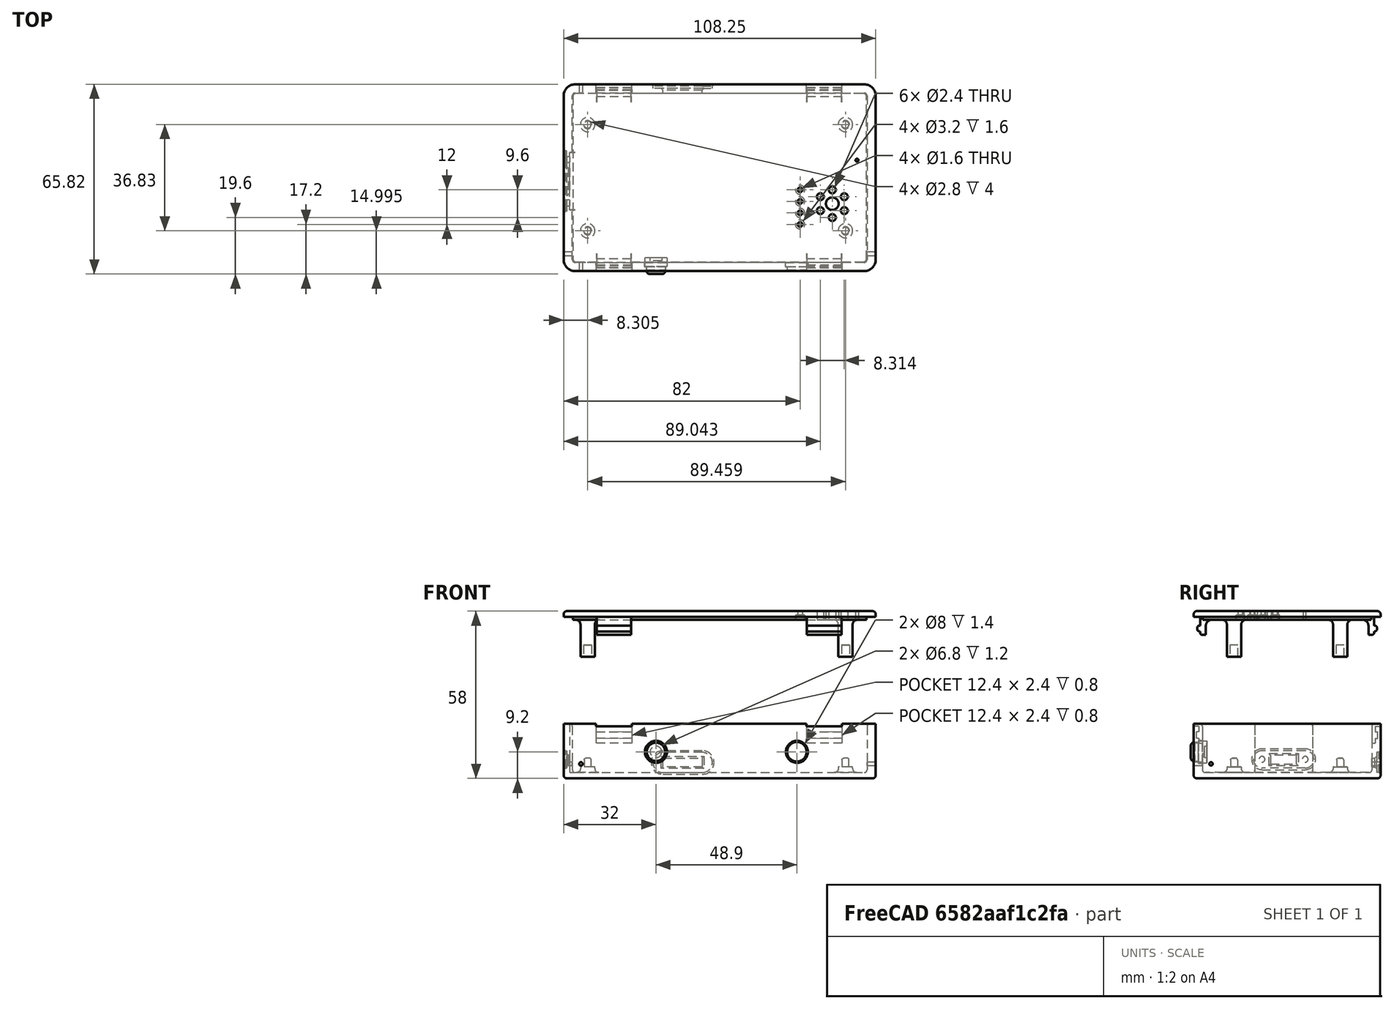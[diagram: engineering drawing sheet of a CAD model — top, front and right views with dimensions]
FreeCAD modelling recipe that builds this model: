
FCSTD DOCUMENT  (FreeCAD 0.17R13541 (Git))
Label: Variometer-Case
License: All rights reserved
LicenseURL: http://en.wikipedia.org/wiki/All_rights_reserved
objects: Sketcher::SketchObject×29, PartDesign::Pocket×17, PartDesign::Fillet×17, PartDesign::Plane×12, PartDesign::Pad×11, PartDesign::Body×4, Mesh::Feature×4, PartDesign::ShapeBinder×3, PartDesign::Chamfer×3
note: 124 computed .brp shape members not serialized (recipe doc carries the construction recipe); baked Part::Feature solids carry a one-line shape summary decoded from their .brp

FEATURE [Sketcher::SketchObject] Sketch  label="MasterSketch"
  MapMode = 5
  Support = -> [XY_Plane]
  sketch-geometry (27):
    g0: LineSegment StartX=0 StartY=58.42 StartZ=0 EndX=101.85 EndY=58.42 EndZ=0
    g1: LineSegment StartX=101.85 StartY=58.42 StartZ=0 EndX=101.85 EndY=0 EndZ=0
    g2: LineSegment StartX=101.85 StartY=0 StartZ=0 EndX=0 EndY=0 EndZ=0
    g3: LineSegment StartX=0 StartY=0 StartZ=0 EndX=0 EndY=58.42 EndZ=0
    g4: Circle CenterX=5.105 CenterY=10.795 CenterZ=0 NormalX=0 NormalY=0 NormalZ=1 AngleXU=0 Radius=2.5
    g5: Circle CenterX=5.105 CenterY=47.625 CenterZ=0 NormalX=0 NormalY=0 NormalZ=1 AngleXU=0 Radius=2.5
    g6: Circle CenterX=94.564 CenterY=10.795 CenterZ=0 NormalX=0 NormalY=0 NormalZ=1 AngleXU=0 Radius=2.5
    g7: Circle CenterX=94.564 CenterY=47.625 CenterZ=0 NormalX=0 NormalY=0 NormalZ=1 AngleXU=0 Radius=2.5
    g8: LineSegment StartX=28.3 StartY=53.4492 StartZ=0 EndX=28.3 EndY=63.3867 EndZ=0
    g9: LineSegment StartX=11.3 StartY=63.3867 StartZ=0 EndX=11.3 EndY=53.4492 EndZ=0
    g10: Circle CenterX=90 CenterY=20.2 CenterZ=0 NormalX=0 NormalY=0 NormalZ=1 AngleXU=0 Radius=7
    g11: Circle CenterX=78.8 CenterY=25 CenterZ=0 NormalX=0 NormalY=0 NormalZ=1 AngleXU=0 Radius=1
    g12: Circle CenterX=78.8 CenterY=21 CenterZ=0 NormalX=0 NormalY=0 NormalZ=1 AngleXU=0 Radius=1
    g13: Circle CenterX=78.8 CenterY=17 CenterZ=0 NormalX=0 NormalY=0 NormalZ=1 AngleXU=0 Radius=1
    g14: Circle CenterX=78.8 CenterY=13 CenterZ=0 NormalX=0 NormalY=0 NormalZ=1 AngleXU=0 Radius=1
    g15: Circle CenterX=98.56 CenterY=35.28 CenterZ=0 NormalX=0 NormalY=0 NormalZ=1 AngleXU=0 Radius=1
    g16: LineSegment StartX=46.46 StartY=63.8315 StartZ=0 EndX=46.46 EndY=53.6528 EndZ=0
    g17: LineSegment StartX=31.26 StartY=53.6528 StartZ=0 EndX=31.26 EndY=63.3799 EndZ=0
    g18: LineSegment StartX=164.118 StartY=59.2092 StartZ=0 EndX=164.118 EndY=40.2092 EndZ=0
    g19: LineSegment StartX=176.88 StartY=59.5541 StartZ=0 EndX=176.88 EndY=42.5541 EndZ=0
    g20: LineSegment StartX=-10.0374 StartY=20.5 StartZ=0 EndX=4.83678 EndY=20.5 EndZ=0
    g21: LineSegment StartX=-10.1738 StartY=28 StartZ=0 EndX=4.42739 EndY=28 EndZ=0
    g22: LineSegment StartX=-10.0374 StartY=35.5 StartZ=0 EndX=4.56386 EndY=35.5 EndZ=0
    g23: LineSegment StartX=28.8 StartY=5.89163 StartZ=0 EndX=28.8 EndY=-5.34826 EndZ=0
    g24: LineSegment StartX=77.7 StartY=5.89163 StartZ=0 EndX=77.7 EndY=-5.48472 EndZ=0
    g25: LineSegment StartX=8 StartY=6.13746 StartZ=0 EndX=8 EndY=-25.1864 EndZ=0
    g26: LineSegment StartX=81 StartY=5.59162 StartZ=0 EndX=81 EndY=-24.8827 EndZ=0
  constraints (67):
    c: Coincident(g0,g1)
    c: Coincident(g1,g2)
    c: Coincident(g2,g3)
    c: Coincident(g3,g0)
    c: Horizontal(g0)
    c: Horizontal(g2)
    c: Vertical(g1)
    c: Vertical(g3)
    c: DistanceX(g0,g0) = 101.85  'PCB_Width'
    c: DistanceY(g1,g1) = 58.42  'PCB_Height'
    c: Coincident(g2,g-1)
    c: DistanceX(g-1,g4) = 5.105
    c: Vertical(g4,g5)
    c: DistanceY(g-1,g4) = 10.795
    c: DistanceY(g-1,g5) = 47.625
    c: DistanceX(g-1,g6) = 94.564
    c: Vertical(g6,g7)
    c: Horizontal(g4,g6)
    c: Horizontal(g5,g7)
    c: Radius(g5) = 2.5  'PCBSupporterRadius'
    c: Equal(g5,g4)
    c: Equal(g5,g6)
    c: Equal(g5,g7)
    c: Vertical(g8)
    c: Vertical(g9)
    c: DistanceX(g-1,g10) = 90
    c: DistanceY(g-1,g10) = 20.2
    c: Radius(g10) = 7
    c: Vertical(g14,g13)
    c: Vertical(g13,g12)
    c: Vertical(g12,g11)
    c: DistanceX(g-1,g14) = 78.8
    c: Radius(g14) = 1
    c: Equal(g14,g13)
    c: Equal(g14,g12)
    c: Equal(g14,g11)
    c: DistanceY(g1,g14) = 13
    c: DistanceY(g1,g13) = 17
    c: DistanceY(g1,g12) = 21
    c: DistanceY(g1,g11) = 25
    c: DistanceX(g-1,g15) = 98.56
    c: DistanceY(g1,g15) = 35.28
    c: Vertical(g16)
    c: Vertical(g17)
    c: DistanceX(g-1,g17) = 31.26  'BT_X1'
    c: Radius(g15) = 1
    c: Vertical(g18)
    c: Vertical(g19)
    c: DistanceY(g18,g18) = 19  'totalHeight'
    c: DistanceY(g19,g19) = 17  'innerDepth'
    c: Horizontal(g20)
    c: Horizontal(g21)
    c: Horizontal(g22)
    c: DistanceY(g-1,g20) = 20.5  'ledGreeHeight'
    c: DistanceY(g-1,g21) = 28  'USBPos'
    c: DistanceY(g-1,g22) = 35.5  'RedLEDPos'
    c: Vertical(g23)
    c: Vertical(g24)
    c: DistanceX(g-1,g23) = 28.8
    c: DistanceX(g-1,g24) = 77.7
    c: DistanceX(g0,g16) = 46.46  'BT_X2'
    c: DistanceX(g0,g9) = 11.3  'IMU_X1'
    c: DistanceX(g0,g8) = 28.3  'IMU_X2'
    c: Vertical(g25)
    c: Vertical(g26)
    c: DistanceX(g-1,g25) = 8  'Locker_X1'
    c: DistanceX(g-1,g26) = 81  'Locker_X2'
FEATURE [PartDesign::Body] Body  label="MasterBlock"
  Group = -> [Sketch]
  Origin = -> Origin
FEATURE [PartDesign::ShapeBinder] ShapeBinder  label="BodyShapeBinder"
  Support = -> [Sketch]
FEATURE [Sketcher::SketchObject] Sketch001  label="Outer"
  ExternalGeometry = -> [ShapeBinder]
  MapMode = 5
  Support = -> [XY_Plane001]
  sketch-geometry (4):
    g0: LineSegment StartX=-3.2 StartY=61.62 StartZ=0 EndX=105.05 EndY=61.62 EndZ=0
    g1: LineSegment StartX=105.05 StartY=61.62 StartZ=0 EndX=105.05 EndY=-3.2 EndZ=0
    g2: LineSegment StartX=105.05 StartY=-3.2 StartZ=0 EndX=-3.2 EndY=-3.2 EndZ=0
    g3: LineSegment StartX=-3.2 StartY=-3.2 StartZ=0 EndX=-3.2 EndY=61.62 EndZ=0
  constraints (12):
    c: Coincident(g0,g1)
    c: Coincident(g1,g2)
    c: Coincident(g2,g3)
    c: Coincident(g3,g0)
    c: Horizontal(g0)
    c: Horizontal(g2)
    c: Vertical(g1)
    c: Vertical(g3)
    c: DistanceY(g2,g-1) = 3.2
    c: DistanceX(g2,g-1) = 3.2
    c: DistanceX(g-3,g0) = 3.2
    c: DistanceY(g-3,g0) = 3.2
FEATURE [PartDesign::Pad] Pad  label="OuterBlock"
  Length = 19
  Length2 = 100
  Profile = -> Sketch001
  Type = 0
  expr: Length = 19
FEATURE [PartDesign::Plane] DatumPlane  label="UpperPlane"
  MapMode = 45
  Placement = pos=(50.925,29.21,19) rot=(0,0,1;1.5708rad)
  Support = -> [Pad]
FEATURE [Sketcher::SketchObject] Sketch002  label="Inner"
  ExternalGeometry = -> [Pad]
  MapMode = 5
  Placement = pos=(50.925,29.21,19) rot=(0,0,1;1.5708rad)
  Support = -> [DatumPlane]
  sketch-geometry (4):
    g0: LineSegment StartX=-29.41 StartY=51.125 StartZ=0 EndX=29.41 EndY=51.125 EndZ=0
    g1: LineSegment StartX=29.41 StartY=51.125 StartZ=0 EndX=29.41 EndY=-51.125 EndZ=0
    g2: LineSegment StartX=29.41 StartY=-51.125 StartZ=0 EndX=-29.41 EndY=-51.125 EndZ=0
    g3: LineSegment StartX=-29.41 StartY=-51.125 StartZ=0 EndX=-29.41 EndY=51.125 EndZ=0
  constraints (12):
    c: Coincident(g0,g1)
    c: Coincident(g1,g2)
    c: Coincident(g2,g3)
    c: Coincident(g3,g0)
    c: Horizontal(g0)
    c: Horizontal(g2)
    c: Vertical(g1)
    c: Vertical(g3)
    c: DistanceY(g0,g-3) = 3
    c: DistanceX(g-3,g0) = 3
    c: DistanceX(g1,g-4) = 3
    c: DistanceY(g-4,g1) = 3
FEATURE [PartDesign::Pocket] Pocket  label="InnerBlock"
  BaseFeature = -> Pad
  Length = 17
  Length2 = 100
  Profile = -> Sketch002
  Type = 0
FEATURE [PartDesign::Plane] DatumPlane001  label="InnerBottom"
  MapMode = 5
  Placement = pos=(0,0,2) rot=(0,0,1;0rad)
  Support = -> [Pocket]
FEATURE [Sketcher::SketchObject] Sketch003
  ExternalGeometry = -> [ShapeBinder]
  MapMode = 5
  Placement = pos=(0,0,2) rot=(0,0,1;0rad)
  Support = -> [DatumPlane001]
  sketch-geometry (4):
    g0: Circle CenterX=5.105 CenterY=47.625 CenterZ=0 NormalX=0 NormalY=0 NormalZ=1 AngleXU=0 Radius=2.5
    g1: Circle CenterX=94.564 CenterY=47.625 CenterZ=0 NormalX=0 NormalY=0 NormalZ=1 AngleXU=0 Radius=2.5
    g2: Circle CenterX=94.564 CenterY=10.795 CenterZ=0 NormalX=0 NormalY=0 NormalZ=1 AngleXU=0 Radius=2.5
    g3: Circle CenterX=5.105 CenterY=10.795 CenterZ=0 NormalX=0 NormalY=0 NormalZ=1 AngleXU=0 Radius=2.5
  constraints (8):
    c: Coincident(g0,g-5)
    c: Coincident(g1,g-4)
    c: Coincident(g2,g-3)
    c: Coincident(g3,g-6)
    c: Equal(g3,g0)
    c: Equal(g0,g1)
    c: Equal(g1,g2)
    c: Radius(g3) = 2.5
FEATURE [PartDesign::Pad] Pad001  label="PCBSupporter"
  BaseFeature = -> Pocket
  Length = 2
  Length2 = 100
  Profile = -> Sketch003
  Type = 0
FEATURE [PartDesign::Plane] DatumPlane002  label="PCBPlane"
  MapMode = 5
  Placement = pos=(0,0,4) rot=(0,0,1;0rad)
  Support = -> [Pad001]
FEATURE [Sketcher::SketchObject] Sketch004
  ExternalGeometry = -> [Pad001]
  MapMode = 5
  Placement = pos=(0,0,4) rot=(0,0,1;0rad)
  Support = -> [DatumPlane002]
  sketch-geometry (4):
    g0: Circle CenterX=5.105 CenterY=47.625 CenterZ=0 NormalX=0 NormalY=0 NormalZ=1 AngleXU=0 Radius=1.2
    g1: Circle CenterX=94.564 CenterY=47.625 CenterZ=0 NormalX=0 NormalY=0 NormalZ=1 AngleXU=0 Radius=1.2
    g2: Circle CenterX=94.564 CenterY=10.795 CenterZ=0 NormalX=0 NormalY=0 NormalZ=1 AngleXU=0 Radius=1.2
    g3: Circle CenterX=5.105 CenterY=10.795 CenterZ=0 NormalX=0 NormalY=0 NormalZ=1 AngleXU=0 Radius=1.2
  constraints (8):
    c: Coincident(g0,g-6)
    c: Coincident(g1,g-3)
    c: Coincident(g3,g-5)
    c: Coincident(g-4,g2)
    c: Equal(g0,g3)
    c: Equal(g3,g2)
    c: Equal(g2,g1)
    c: Radius(g0) = 1.2
FEATURE [PartDesign::Pad] Pad002  label="PCBHole"
  BaseFeature = -> Pad001
  Length = 3
  Length2 = 100
  Profile = -> Sketch004
  Type = 0
FEATURE [PartDesign::Plane] DatumPlane003  label="LeftSideInnerPlane"
  MapMode = 5
  Placement = pos=(0,58.62,0) rot=(1,0,0;1.5708rad)
  Support = -> [Pad002]
FEATURE [PartDesign::Plane] DatumPlane004  label="RightSideInnerPlane"
  MapMode = 5
  Placement = pos=(0,-0.2,0) rot=(0,0.707107,0.707107;3.14159rad)
  Support = -> [Pad002]
FEATURE [PartDesign::Plane] DatumPlane005  label="LowerSideInnerPlane"
  MapMode = 5
  Placement = pos=(-0.2,0,0) rot=(0.57735,0.57735,0.57735;2.0944rad)
  Support = -> [Pad002]
FEATURE [Sketcher::SketchObject] Sketch005  label="LeftSideInnerHoles"
  ExternalGeometry = -> [ShapeBinder,Pad002]
  MapMode = 5
  Placement = pos=(0,58.62,0) rot=(1,0,0;1.5708rad)
  Support = -> [DatumPlane003]
  sketch-geometry (12):
    g0: LineSegment StartX=8 StartY=19 StartZ=0 EndX=20.4 EndY=19 EndZ=0
    g1: LineSegment StartX=20.4 StartY=19 StartZ=0 EndX=20.4 EndY=18 EndZ=0
    g2: LineSegment StartX=20.4 StartY=18 StartZ=0 EndX=8 EndY=18 EndZ=0
    g3: LineSegment StartX=8 StartY=18 StartZ=0 EndX=8 EndY=19 EndZ=0
    g4: LineSegment StartX=81 StartY=19 StartZ=0 EndX=93.4 EndY=19 EndZ=0
    g5: LineSegment StartX=93.4 StartY=19 StartZ=0 EndX=93.4 EndY=18 EndZ=0
    g6: LineSegment StartX=93.4 StartY=18 StartZ=0 EndX=81 EndY=18 EndZ=0
    g7: LineSegment StartX=81 StartY=18 StartZ=0 EndX=81 EndY=19 EndZ=0
    g8: LineSegment StartX=31.26 StartY=7 StartZ=0 EndX=44.86 EndY=7 EndZ=0
    g9: LineSegment StartX=44.86 StartY=7 StartZ=0 EndX=44.86 EndY=4 EndZ=0
    g10: LineSegment StartX=44.86 StartY=4 StartZ=0 EndX=31.26 EndY=4 EndZ=0
    g11: LineSegment StartX=31.26 StartY=4 StartZ=0 EndX=31.26 EndY=7 EndZ=0
  constraints (36):
    c: Coincident(g0,g1)
    c: Coincident(g1,g2)
    c: Coincident(g2,g3)
    c: Coincident(g3,g0)
    c: Horizontal(g0)
    c: Horizontal(g2)
    c: Vertical(g1)
    c: Vertical(g3)
    c: Coincident(g4,g5)
    c: Coincident(g5,g6)
    c: Coincident(g6,g7)
    c: Coincident(g7,g4)
    c: Horizontal(g4)
    c: Horizontal(g6)
    c: Vertical(g5)
    c: Vertical(g7)
    c: Coincident(g8,g9)
    c: Coincident(g9,g10)
    c: Coincident(g10,g11)
    c: Coincident(g11,g8)
    c: Horizontal(g8)
    c: Horizontal(g10)
    c: Vertical(g9)
    c: Vertical(g11)
    c: Vertical(g-5,g2)
    c: Vertical(g-7,g6)
    c: Equal(g0,g4)
    c: Equal(g1,g5)
    c: Tangent(g0,g-6) = 1.5708
    c: PointOnObject(g4,g-6)
    c: Distance(g1) = 1
    c: Distance(g0) = 12.4
    c: Vertical(g-3,g10)
    c: DistanceY(g9,g9) = 3
    c: DistanceY(g-4,g9) = 4
    c: DistanceX(g8,g8) = 13.6
FEATURE [PartDesign::Pocket] Pocket001  label="LeftSideThroughHole"
  BaseFeature = -> Pad002
  Length = 5
  Length2 = 100
  Profile = -> Sketch005
  Type = 1
FEATURE [Sketcher::SketchObject] Sketch006  label="RightSideInnerHoles"
  ExternalGeometry = -> [ShapeBinder,Pocket001]
  MapMode = 5
  Placement = pos=(0,-0.2,0) rot=(0,0.707107,0.707107;3.14159rad)
  Support = -> [DatumPlane004]
  sketch-geometry (10):
    g0: LineSegment StartX=-93.4 StartY=19 StartZ=0 EndX=-81 EndY=19 EndZ=0
    g1: LineSegment StartX=-81 StartY=19 StartZ=0 EndX=-81 EndY=18 EndZ=0
    g2: LineSegment StartX=-81 StartY=18 StartZ=0 EndX=-93.4 EndY=18 EndZ=0
    g3: LineSegment StartX=-93.4 StartY=18 StartZ=0 EndX=-93.4 EndY=19 EndZ=0
    g4: LineSegment StartX=-20.4 StartY=19 StartZ=0 EndX=-8 EndY=19 EndZ=0
    g5: LineSegment StartX=-8 StartY=19 StartZ=0 EndX=-8 EndY=18 EndZ=0
    g6: LineSegment StartX=-8 StartY=18 StartZ=0 EndX=-20.4 EndY=18 EndZ=0
    g7: LineSegment StartX=-20.4 StartY=18 StartZ=0 EndX=-20.4 EndY=19 EndZ=0
    g8: Circle CenterX=-77.7 CenterY=9.2 CenterZ=0 NormalX=0 NormalY=0 NormalZ=1 AngleXU=0 Radius=3.4
    g9: Circle CenterX=-28.8 CenterY=9.2 CenterZ=0 NormalX=0 NormalY=0 NormalZ=1 AngleXU=0 Radius=3.4
  constraints (30):
    c: Coincident(g0,g1)
    c: Coincident(g1,g2)
    c: Coincident(g2,g3)
    c: Coincident(g3,g0)
    c: Horizontal(g0)
    c: Horizontal(g2)
    c: Vertical(g1)
    c: Vertical(g3)
    c: Coincident(g4,g5)
    c: Coincident(g5,g6)
    c: Coincident(g6,g7)
    c: Coincident(g7,g4)
    c: Horizontal(g4)
    c: Horizontal(g6)
    c: Vertical(g5)
    c: Vertical(g7)
    c: PointOnObject(g0,g-7)
    c: PointOnObject(g4,g-7)
    c: Vertical(g-6,g1)
    c: Vertical(g-5,g5)
    c: Equal(g7,g3)
    c: DistanceY(g1,g1) = 1
    c: DistanceX(g0,g0) = 12.4
    c: Equal(g8,g9)
    c: Radius(g9) = 3.4
    c: Equal(g4,g0)
    c: Vertical(g-3,g8)
    c: Vertical(g-4,g9)
    c: Horizontal(g8,g9)
    c: DistanceY(g-4,g9) = 9.2
FEATURE [PartDesign::Pocket] Pocket002  label="RightSideThroughHole"
  BaseFeature = -> Pocket001
  Length = 5
  Length2 = 100
  Profile = -> Sketch006
  Type = 1
FEATURE [Sketcher::SketchObject] Sketch007  label="FrontSideInnderHoles"
  ExternalGeometry = -> [ShapeBinder]
  MapMode = 5
  Placement = pos=(-0.2,0,0) rot=(0.57735,0.57735,0.57735;2.0944rad)
  Support = -> [DatumPlane005]
  sketch-geometry (8):
    g0: Circle CenterX=20.5 CenterY=6.6 CenterZ=0 NormalX=0 NormalY=0 NormalZ=1 AngleXU=0 Radius=1
    g1: Circle CenterX=35.5 CenterY=6.6 CenterZ=0 NormalX=0 NormalY=0 NormalZ=1 AngleXU=0 Radius=1
    g2: LineSegment StartX=23.5 StartY=8 StartZ=0 EndX=32.5 EndY=8 EndZ=0
    g3: LineSegment StartX=32.5 StartY=8 StartZ=0 EndX=32.5 EndY=5 EndZ=0
    g4: LineSegment StartX=32.5 StartY=5 StartZ=0 EndX=23.5 EndY=5 EndZ=0
    g5: LineSegment StartX=23.5 StartY=5 StartZ=0 EndX=23.5 EndY=8 EndZ=0
    g6: LineSegment [constr] StartX=28 StartY=0 StartZ=0 EndX=28 EndY=13.3312 EndZ=0
    g7: LineSegment [constr] StartX=13.8871 StartY=5 StartZ=0 EndX=41.4899 EndY=5 EndZ=0
  constraints (22):
    c: Coincident(g2,g3)
    c: Coincident(g3,g4)
    c: Coincident(g4,g5)
    c: Coincident(g5,g2)
    c: Horizontal(g2)
    c: Horizontal(g4)
    c: Vertical(g3)
    c: Vertical(g5)
    c: Coincident(g6,g-3)
    c: Vertical(g6)
    c: Horizontal(g7)
    c: DistanceY(g-4,g7) = 5
    c: Symmetric(g2,g2,g6)
    c: DistanceX(g2,g2) = 9
    c: Vertical(g1,g-4)
    c: Vertical(g-5,g0)
    c: Horizontal(g0,g1)
    c: Equal(g0,g1)
    c: Radius(g0) = 1
    c: PointOnObject(g3,g7)
    c: DistanceY(g3,g3) = 3
    c: DistanceY(g4,g0) = 1.6
FEATURE [PartDesign::Pocket] Pocket003  label="FrontSideThroughHole"
  BaseFeature = -> Pocket002
  Length = 5
  Length2 = 100
  Profile = -> Sketch007
  Type = 1
FEATURE [PartDesign::Plane] DatumPlane006  label="RightSideOuterPlane"
  MapMode = 5
  Placement = pos=(0,61.62,0) rot=(0,0.707107,0.707107;3.14159rad)
  Support = -> [Pocket003]
FEATURE [PartDesign::Plane] DatumPlane007  label="LowerSideOuterPlane"
  MapMode = 5
  Placement = pos=(-3.2,0,0) rot=(0.57735,-0.57735,-0.57735;2.0944rad)
  Support = -> [Pocket003]
FEATURE [Sketcher::SketchObject] Sketch008  label="LockerHole"
  ExternalGeometry = -> [Pocket003]
  MapMode = 5
  Placement = pos=(50.925,29.21,19) rot=(0,0,1;1.5708rad)
  Support = -> [DatumPlane]
  sketch-geometry (16):
    g0: LineSegment StartX=-30.61 StartY=42.925 StartZ=0 EndX=-29.41 EndY=42.925 EndZ=0
    g1: LineSegment StartX=-29.41 StartY=42.925 StartZ=0 EndX=-29.41 EndY=30.525 EndZ=0
    g2: LineSegment StartX=-29.41 StartY=30.525 StartZ=0 EndX=-30.61 EndY=30.525 EndZ=0
    g3: LineSegment StartX=-30.61 StartY=30.525 StartZ=0 EndX=-30.61 EndY=42.925 EndZ=0
    g4: LineSegment StartX=29.41 StartY=42.925 StartZ=0 EndX=30.61 EndY=42.925 EndZ=0
    g5: LineSegment StartX=30.61 StartY=42.925 StartZ=0 EndX=30.61 EndY=30.525 EndZ=0
    g6: LineSegment StartX=30.61 StartY=30.525 StartZ=0 EndX=29.41 EndY=30.525 EndZ=0
    g7: LineSegment StartX=29.41 StartY=30.525 StartZ=0 EndX=29.41 EndY=42.925 EndZ=0
    g8: LineSegment StartX=29.41 StartY=-30.075 StartZ=0 EndX=30.61 EndY=-30.075 EndZ=0
    g9: LineSegment StartX=30.61 StartY=-30.075 StartZ=0 EndX=30.61 EndY=-42.475 EndZ=0
    g10: LineSegment StartX=30.61 StartY=-42.475 StartZ=0 EndX=29.41 EndY=-42.475 EndZ=0
    g11: LineSegment StartX=29.41 StartY=-42.475 StartZ=0 EndX=29.41 EndY=-30.075 EndZ=0
    g12: LineSegment StartX=-29.41 StartY=-30.075 StartZ=0 EndX=-30.61 EndY=-30.075 EndZ=0
    g13: LineSegment StartX=-30.61 StartY=-30.075 StartZ=0 EndX=-30.61 EndY=-42.475 EndZ=0
    g14: LineSegment StartX=-30.61 StartY=-42.475 StartZ=0 EndX=-29.41 EndY=-42.475 EndZ=0
    g15: LineSegment StartX=-29.41 StartY=-42.475 StartZ=0 EndX=-29.41 EndY=-30.075 EndZ=0
  constraints (44):
    c: Coincident(g0,g1)
    c: Coincident(g1,g2)
    c: Coincident(g2,g3)
    c: Coincident(g3,g0)
    c: Horizontal(g0)
    c: Horizontal(g2)
    c: Vertical(g1)
    c: Vertical(g3)
    c: Coincident(g4,g5)
    c: Coincident(g5,g6)
    c: Coincident(g6,g7)
    c: Coincident(g7,g4)
    c: Horizontal(g4)
    c: Horizontal(g6)
    c: Vertical(g5)
    c: Vertical(g7)
    c: Coincident(g4,g-4)
    c: Coincident(g8,g9)
    c: Coincident(g9,g10)
    c: Coincident(g10,g11)
    c: Coincident(g11,g8)
    c: Horizontal(g8)
    c: Horizontal(g10)
    c: Vertical(g9)
    c: Vertical(g11)
    c: Coincident(g8,g-5)
    c: Coincident(g12,g13)
    c: Coincident(g13,g14)
    c: Coincident(g14,g15)
    c: Coincident(g15,g12)
    c: Horizontal(g12)
    c: Horizontal(g14)
    c: Vertical(g13)
    c: Vertical(g15)
    c: Coincident(g0,g-3)
    c: Coincident(g1,g-3)
    c: Coincident(g6,g-4)
    c: Coincident(g10,g-5)
    c: Coincident(g12,g-6)
    c: Coincident(g14,g-6)
    c: Equal(g12,g8)
    c: Equal(g8,g2)
    c: Equal(g2,g6)
    c: DistanceX(g2,g2) = 1.2
FEATURE [PartDesign::Pocket] Pocket004  label="LockerInnerPocker"
  BaseFeature = -> Pocket003
  Length = 6.8
  Length2 = 100
  Profile = -> Sketch008
  Type = 0
FEATURE [Sketcher::SketchObject] Sketch009  label="LeftSideLockingHole"
  ExternalGeometry = -> [Pocket004]
  MapMode = 5
  Placement = pos=(0,58.62,0) rot=(1,0,0;1.5708rad)
  Support = -> [DatumPlane003]
  sketch-geometry (8):
    g0: LineSegment StartX=8 StartY=16.2 StartZ=0 EndX=20.4 EndY=16.2 EndZ=0
    g1: LineSegment StartX=20.4 StartY=16.2 StartZ=0 EndX=20.4 EndY=13.8 EndZ=0
    g2: LineSegment StartX=20.4 StartY=13.8 StartZ=0 EndX=8 EndY=13.8 EndZ=0
    g3: LineSegment StartX=8 StartY=13.8 StartZ=0 EndX=8 EndY=16.2 EndZ=0
    g4: LineSegment StartX=81 StartY=16.2 StartZ=0 EndX=93.4 EndY=16.2 EndZ=0
    g5: LineSegment StartX=93.4 StartY=16.2 StartZ=0 EndX=93.4 EndY=13.8 EndZ=0
    g6: LineSegment StartX=93.4 StartY=13.8 StartZ=0 EndX=81 EndY=13.8 EndZ=0
    g7: LineSegment StartX=81 StartY=13.8 StartZ=0 EndX=81 EndY=16.2 EndZ=0
  constraints (24):
    c: Coincident(g0,g1)
    c: Coincident(g1,g2)
    c: Coincident(g2,g3)
    c: Coincident(g3,g0)
    c: Horizontal(g0)
    c: Horizontal(g2)
    c: Vertical(g1)
    c: Vertical(g3)
    c: Coincident(g4,g5)
    c: Coincident(g5,g6)
    c: Coincident(g6,g7)
    c: Coincident(g7,g4)
    c: Horizontal(g4)
    c: Horizontal(g6)
    c: Vertical(g5)
    c: Vertical(g7)
    c: Vertical(g-3,g0)
    c: Vertical(g-3,g0)
    c: Vertical(g-4,g4)
    c: Vertical(g-4,g4)
    c: Equal(g1,g7)
    c: DistanceY(g0,g-3) = 1.8
    c: DistanceY(g1,g0) = 2.4
    c: Horizontal(g4,g0)
FEATURE [PartDesign::Pocket] Pocket005  label="LeftSideLockingHolePocket"
  BaseFeature = -> Pocket004
  Length = 2
  Length2 = 100
  Profile = -> Sketch009
  Type = 0
FEATURE [Sketcher::SketchObject] Sketch010  label="RightSideLockingHole"
  ExternalGeometry = -> [Pocket005]
  MapMode = 5
  Placement = pos=(0,-0.2,0) rot=(0,0.707107,0.707107;3.14159rad)
  Support = -> [DatumPlane004]
  sketch-geometry (8):
    g0: LineSegment StartX=-93.4 StartY=16.2 StartZ=0 EndX=-81 EndY=16.2 EndZ=0
    g1: LineSegment StartX=-81 StartY=16.2 StartZ=0 EndX=-81 EndY=13.8 EndZ=0
    g2: LineSegment StartX=-81 StartY=13.8 StartZ=0 EndX=-93.4 EndY=13.8 EndZ=0
    g3: LineSegment StartX=-93.4 StartY=13.8 StartZ=0 EndX=-93.4 EndY=16.2 EndZ=0
    g4: LineSegment StartX=-20.4 StartY=16.2 StartZ=0 EndX=-8 EndY=16.2 EndZ=0
    g5: LineSegment StartX=-8 StartY=16.2 StartZ=0 EndX=-8 EndY=13.8 EndZ=0
    g6: LineSegment StartX=-8 StartY=13.8 StartZ=0 EndX=-20.4 EndY=13.8 EndZ=0
    g7: LineSegment StartX=-20.4 StartY=13.8 StartZ=0 EndX=-20.4 EndY=16.2 EndZ=0
  constraints (24):
    c: Coincident(g0,g1)
    c: Coincident(g1,g2)
    c: Coincident(g2,g3)
    c: Coincident(g3,g0)
    c: Horizontal(g0)
    c: Horizontal(g2)
    c: Vertical(g1)
    c: Vertical(g3)
    c: Coincident(g4,g5)
    c: Coincident(g5,g6)
    c: Coincident(g6,g7)
    c: Coincident(g7,g4)
    c: Horizontal(g4)
    c: Horizontal(g6)
    c: Vertical(g5)
    c: Vertical(g7)
    c: Horizontal(g0,g4)
    c: Vertical(g0,g-3)
    c: Vertical(g-3,g0)
    c: Vertical(g-4,g4)
    c: Vertical(g-4,g4)
    c: DistanceY(g0,g-3) = 1.8
    c: Distance(g1) = 2.4
    c: Equal(g1,g7)
FEATURE [PartDesign::Pocket] Pocket006  label="RightSideLockingHolePocket"
  BaseFeature = -> Pocket005
  Length = 2
  Length2 = 100
  Profile = -> Sketch010
  Type = 0
FEATURE [Sketcher::SketchObject] Sketch011  label="KeyOuter"
  ExternalGeometry = -> [Pocket006]
  MapMode = 5
  Placement = pos=(0,-0.2,0) rot=(0,0.707107,0.707107;3.14159rad)
  Support = -> [DatumPlane004]
  sketch-geometry (2):
    g0: Circle CenterX=-77.7 CenterY=9.2 CenterZ=0 NormalX=0 NormalY=0 NormalZ=1 AngleXU=0 Radius=4
    g1: Circle CenterX=-28.8 CenterY=9.2 CenterZ=0 NormalX=0 NormalY=0 NormalZ=1 AngleXU=0 Radius=4
  constraints (4):
    c: Coincident(g0,g-4)
    c: Coincident(g1,g-3)
    c: Equal(g1,g0)
    c: Radius(g1) = 4
FEATURE [PartDesign::Pocket] Pocket007  label="KeyOuterPocket"
  BaseFeature = -> Pocket006
  Length = 1.4
  Length2 = 100
  Profile = -> Sketch011
  Type = 0
FEATURE [PartDesign::ShapeBinder] ShapeBinder001  label="CoverShapeBinder"
  Support = -> [Sketch]
FEATURE [PartDesign::Plane] DatumPlane008  label="CoverBasePlane"
  AttachmentOffset = pos=(0,0,49) rot=(0,0,1;0rad)
  MapMode = 45
  Placement = pos=(50.925,29.21,49) rot=(0,0,1;1.5708rad)
  Support = -> [ShapeBinder001]
FEATURE [Sketcher::SketchObject] Sketch012  label="CoverOuter"
  ExternalGeometry = -> [ShapeBinder001]
  MapMode = 5
  Placement = pos=(50.925,29.21,49) rot=(0,0,1;1.5708rad)
  Support = -> [DatumPlane008]
  sketch-geometry (4):
    g0: LineSegment StartX=-32.41 StartY=54.125 StartZ=0 EndX=32.41 EndY=54.125 EndZ=0
    g1: LineSegment StartX=32.41 StartY=54.125 StartZ=0 EndX=32.41 EndY=-54.125 EndZ=0
    g2: LineSegment StartX=32.41 StartY=-54.125 StartZ=0 EndX=-32.41 EndY=-54.125 EndZ=0
    g3: LineSegment StartX=-32.41 StartY=-54.125 StartZ=0 EndX=-32.41 EndY=54.125 EndZ=0
  constraints (12):
    c: Coincident(g0,g1)
    c: Coincident(g1,g2)
    c: Coincident(g2,g3)
    c: Coincident(g3,g0)
    c: Horizontal(g0)
    c: Horizontal(g2)
    c: Vertical(g1)
    c: Vertical(g3)
    c: DistanceY(g-3,g0) = 3.2
    c: DistanceX(g0,g-3) = 3.2
    c: DistanceY(g1,g-5) = 3.2
    c: DistanceX(g-5,g1) = 3.2
FEATURE [PartDesign::Pad] Pad003  label="CoverOuterBlock"
  Length = 2
  Length2 = 100
  Placement = pos=(50.925,29.21,49) rot=(0,0,1;1.5708rad)
  Profile = -> Sketch012
  Type = 0
FEATURE [Sketcher::SketchObject] Sketch017  label="CoverInner"
  ExternalGeometry = -> [Pad003]
  MapMode = 5
  Placement = pos=(50.925,29.21,49) rot=(0.707107,0.707107,0;3.14159rad)
  Support = -> [Pad003]
  sketch-geometry (4):
    g0: LineSegment StartX=-29.21 StartY=50.925 StartZ=0 EndX=29.21 EndY=50.925 EndZ=0
    g1: LineSegment StartX=29.21 StartY=50.925 StartZ=0 EndX=29.21 EndY=-50.925 EndZ=0
    g2: LineSegment StartX=29.21 StartY=-50.925 StartZ=0 EndX=-29.21 EndY=-50.925 EndZ=0
    g3: LineSegment StartX=-29.21 StartY=-50.925 StartZ=0 EndX=-29.21 EndY=50.925 EndZ=0
  constraints (12):
    c: Coincident(g0,g1)
    c: Coincident(g1,g2)
    c: Coincident(g2,g3)
    c: Coincident(g3,g0)
    c: Horizontal(g0)
    c: Horizontal(g2)
    c: Vertical(g1)
    c: Vertical(g3)
    c: DistanceX(g-4,g0) = 3.2
    c: DistanceY(g0,g-4) = 3.2
    c: DistanceY(g-3,g1) = 3.2
    c: DistanceX(g1,g-3) = 3.2
FEATURE [PartDesign::Pad] Pad004  label="ConerInnerBlock"
  BaseFeature = -> Pad003
  Length = 1
  Length2 = 100
  Placement = pos=(50.925,29.21,49) rot=(0,0,1;1.5708rad)
  Profile = -> Sketch017
  Type = 0
FEATURE [PartDesign::Plane] DatumPlane009  label="CoverInnerPlane"
  MapMode = 5
  Placement = pos=(50.925,29.21,48) rot=(0.707107,0.707107,0;3.14159rad)
  Support = -> [Pad004]
FEATURE [Sketcher::SketchObject] Sketch018  label="CoverPCBSupport"
  ExternalGeometry = -> [ShapeBinder001]
  MapMode = 5
  Placement = pos=(50.925,29.21,48) rot=(0.707107,0.707107,0;3.14159rad)
  Support = -> [DatumPlane009]
  sketch-geometry (4):
    g0: Circle CenterX=-18.415 CenterY=43.639 CenterZ=0 NormalX=0 NormalY=0 NormalZ=1 AngleXU=0 Radius=2.5
    g1: Circle CenterX=18.415 CenterY=43.639 CenterZ=0 NormalX=0 NormalY=0 NormalZ=1 AngleXU=0 Radius=2.5
    g2: Circle CenterX=-18.415 CenterY=-45.82 CenterZ=0 NormalX=0 NormalY=0 NormalZ=1 AngleXU=0 Radius=2.5
    g3: Circle CenterX=18.415 CenterY=-45.82 CenterZ=0 NormalX=0 NormalY=0 NormalZ=1 AngleXU=0 Radius=2.5
  constraints (8):
    c: Coincident(g0,g-3)
    c: Coincident(g1,g-4)
    c: Coincident(g2,g-6)
    c: Coincident(g3,g-5)
    c: Equal(g2,g3)
    c: Equal(g3,g0)
    c: Equal(g0,g1)
    c: Radius(g1) = 2.5
FEATURE [PartDesign::Pad] Pad005  label="CoverPCBSupportPad"
  BaseFeature = -> Pad004
  Length = 12.8
  Length2 = 100
  Placement = pos=(50.925,29.21,49) rot=(0,0,1;1.5708rad)
  Profile = -> Sketch018
  Type = 0
FEATURE [PartDesign::Plane] DatumPlane010  label="CoverPCBPlane"
  MapMode = 5
  Placement = pos=(50.925,29.21,35.2) rot=(0.707107,0.707107,0;3.14159rad)
  Support = -> [Pad005]
FEATURE [Sketcher::SketchObject] Sketch019  label="CoverPCBHole"
  ExternalGeometry = -> [ShapeBinder001]
  MapMode = 5
  Placement = pos=(50.925,29.21,35.2) rot=(0.707107,0.707107,0;3.14159rad)
  Support = -> [DatumPlane010]
  sketch-geometry (4):
    g0: Circle CenterX=-18.415 CenterY=-45.82 CenterZ=0 NormalX=0 NormalY=0 NormalZ=1 AngleXU=0 Radius=1.4
    g1: Circle CenterX=18.415 CenterY=-45.82 CenterZ=0 NormalX=0 NormalY=0 NormalZ=1 AngleXU=0 Radius=1.4
    g2: Circle CenterX=-18.415 CenterY=43.639 CenterZ=0 NormalX=0 NormalY=0 NormalZ=1 AngleXU=0 Radius=1.4
    g3: Circle CenterX=18.415 CenterY=43.639 CenterZ=0 NormalX=0 NormalY=0 NormalZ=1 AngleXU=0 Radius=1.4
  constraints (8):
    c: Coincident(g0,g-5)
    c: Coincident(g1,g-6)
    c: Coincident(g2,g-3)
    c: Coincident(g3,g-4)
    c: Equal(g2,g3)
    c: Equal(g3,g0)
    c: Equal(g0,g1)
    c: Radius(g3) = 1.4
FEATURE [PartDesign::Pocket] Pocket008  label="CoverPCBHolePocket"
  BaseFeature = -> Pad005
  Length = 4
  Length2 = 100
  Placement = pos=(50.925,29.21,49) rot=(0,0,1;1.5708rad)
  Profile = -> Sketch019
  Type = 0
FEATURE [Sketcher::SketchObject] Sketch020  label="CoverHoles"
  ExternalGeometry = -> [ShapeBinder001]
  MapMode = 5
  Placement = pos=(50.925,29.21,48) rot=(0.707107,0.707107,0;3.14159rad)
  Support = -> [DatumPlane009]
  sketch-geometry (19):
    g0: Circle CenterX=-16.21 CenterY=27.875 CenterZ=0 NormalX=0 NormalY=0 NormalZ=1 AngleXU=0 Radius=0.8
    g1: Circle CenterX=-12.21 CenterY=27.875 CenterZ=0 NormalX=0 NormalY=0 NormalZ=1 AngleXU=0 Radius=0.8
    g2: Circle CenterX=-8.21 CenterY=27.875 CenterZ=0 NormalX=0 NormalY=0 NormalZ=1 AngleXU=0 Radius=0.8
    g3: Circle CenterX=-4.21 CenterY=27.875 CenterZ=0 NormalX=0 NormalY=0 NormalZ=1 AngleXU=0 Radius=0.8
    g4: Circle CenterX=-9.01 CenterY=39.075 CenterZ=0 NormalX=0 NormalY=0 NormalZ=1 AngleXU=0 Radius=2.2
    g5: Circle CenterX=6.07 CenterY=47.635 CenterZ=0 NormalX=0 NormalY=0 NormalZ=1 AngleXU=0 Radius=0.5
    g6: LineSegment [constr] StartX=-6.61 StartY=34.9181 StartZ=0 EndX=-4.21 EndY=39.075 EndZ=0
    g7: LineSegment [constr] StartX=-4.21 StartY=39.075 StartZ=0 EndX=-6.61 EndY=43.2319 EndZ=0
    g8: LineSegment [constr] StartX=-6.61 StartY=43.2319 StartZ=0 EndX=-11.41 EndY=43.2319 EndZ=0
    g9: LineSegment [constr] StartX=-11.41 StartY=43.2319 StartZ=0 EndX=-13.81 EndY=39.075 EndZ=0
    g10: LineSegment [constr] StartX=-13.81 StartY=39.075 StartZ=0 EndX=-11.41 EndY=34.9181 EndZ=0
    g11: LineSegment [constr] StartX=-11.41 StartY=34.9181 StartZ=0 EndX=-6.61 EndY=34.9181 EndZ=0
    g12: Circle [constr] CenterX=-9.01 CenterY=39.075 CenterZ=0 NormalX=0 NormalY=0 NormalZ=1 AngleXU=0 Radius=4.8
    g13: Circle CenterX=-6.61 CenterY=34.9181 CenterZ=0 NormalX=0 NormalY=0 NormalZ=1 AngleXU=0 Radius=1.2
    g14: Circle CenterX=-11.41 CenterY=34.9181 CenterZ=0 NormalX=0 NormalY=0 NormalZ=1 AngleXU=0 Radius=1.2
    g15: Circle CenterX=-13.81 CenterY=39.075 CenterZ=0 NormalX=0 NormalY=0 NormalZ=1 AngleXU=0 Radius=1.2
    g16: Circle CenterX=-11.41 CenterY=43.2319 CenterZ=0 NormalX=0 NormalY=0 NormalZ=1 AngleXU=0 Radius=1.2
    g17: Circle CenterX=-6.61 CenterY=43.2319 CenterZ=0 NormalX=0 NormalY=0 NormalZ=1 AngleXU=0 Radius=1.2
    g18: Circle CenterX=-4.21 CenterY=39.075 CenterZ=0 NormalX=0 NormalY=0 NormalZ=1 AngleXU=0 Radius=1.2
  constraints (40):
    c: Coincident(g0,g-4)
    c: Coincident(g1,g-5)
    c: Coincident(g2,g-6)
    c: Coincident(g3,g-7)
    c: Coincident(g4,g-3)
    c: Coincident(g5,g-8)
    c: Coincident(g6,g7)
    c: Coincident(g7,g8)
    c: Coincident(g8,g9)
    c: Coincident(g9,g10)
    c: Coincident(g10,g11)
    c: Coincident(g11,g6)
    c: Equal(g6, g7-g11) x5
    c: PointOnObject(g6,g12)
    c: PointOnObject(g7,g12)
    c: PointOnObject(g8,g12)
    c: PointOnObject(g9,g12)
    c: PointOnObject(g10,g12)
    c: PointOnObject(g11,g12)
    c: Coincident(g12,g4)
    c: Coincident(g13,g6)
    c: Coincident(g14,g10)
    c: Coincident(g15,g9)
    c: Coincident(g16,g8)
    c: Coincident(g17,g7)
    c: Coincident(g18,g6)
    c: Horizontal(g4,g6)
    c: Equal(g15,g16)
    c: Equal(g16,g17)
    c: Equal(g17,g18)
    c: Equal(g18,g13)
    c: Equal(g13,g14)
    c: Equal(g0,g1)
    c: Equal(g1,g2)
    c: Equal(g2,g3)
    c: Radius(g3) = 0.8
    c: Radius(g5) = 0.5
    c: Radius(g4) = 2.2
    c: Radius(g13) = 1.2
    c: Distance(g7) = 4.8
FEATURE [PartDesign::Pocket] Pocket009  label="ConverThroughHoles"
  BaseFeature = -> Pocket008
  Length = 5
  Length2 = 100
  Placement = pos=(50.925,29.21,49) rot=(0,0,1;1.5708rad)
  Profile = -> Sketch020
  Type = 1
FEATURE [PartDesign::Plane] DatumPlane011  label="CoverBelowPlane"
  MapMode = 5
  Placement = pos=(50.925,29.21,49) rot=(0.707107,0.707107,0;3.14159rad)
  Support = -> [Pocket009]
FEATURE [Sketcher::SketchObject] Sketch021  label="CoverLockingBar"
  ExternalGeometry = -> [ShapeBinder001]
  MapMode = 5
  Placement = pos=(50.925,29.21,49) rot=(0.707107,0.707107,0;3.14159rad)
  Support = -> [DatumPlane011]
  sketch-geometry (16):
    g0: LineSegment StartX=-30.21 StartY=-30.725 StartZ=0 EndX=-28.21 EndY=-30.725 EndZ=0
    g1: LineSegment StartX=-28.21 StartY=-30.725 StartZ=0 EndX=-28.21 EndY=-42.725 EndZ=0
    g2: LineSegment StartX=-28.21 StartY=-42.725 StartZ=0 EndX=-30.21 EndY=-42.725 EndZ=0
    g3: LineSegment StartX=-30.21 StartY=-42.725 StartZ=0 EndX=-30.21 EndY=-30.725 EndZ=0
    g4: LineSegment StartX=-30.21 StartY=42.275 StartZ=0 EndX=-28.21 EndY=42.275 EndZ=0
    g5: LineSegment StartX=-28.21 StartY=42.275 StartZ=0 EndX=-28.21 EndY=30.275 EndZ=0
    g6: LineSegment StartX=-28.21 StartY=30.275 StartZ=0 EndX=-30.21 EndY=30.275 EndZ=0
    g7: LineSegment StartX=-30.21 StartY=30.275 StartZ=0 EndX=-30.21 EndY=42.275 EndZ=0
    g8: LineSegment StartX=28.21 StartY=42.275 StartZ=0 EndX=30.21 EndY=42.275 EndZ=0
    g9: LineSegment StartX=30.21 StartY=42.275 StartZ=0 EndX=30.21 EndY=30.275 EndZ=0
    g10: LineSegment StartX=30.21 StartY=30.275 StartZ=0 EndX=28.21 EndY=30.275 EndZ=0
    g11: LineSegment StartX=28.21 StartY=30.275 StartZ=0 EndX=28.21 EndY=42.275 EndZ=0
    g12: LineSegment StartX=28.21 StartY=-30.725 StartZ=0 EndX=30.21 EndY=-30.725 EndZ=0
    g13: LineSegment StartX=30.21 StartY=-30.725 StartZ=0 EndX=30.21 EndY=-42.725 EndZ=0
    g14: LineSegment StartX=30.21 StartY=-42.725 StartZ=0 EndX=28.21 EndY=-42.725 EndZ=0
    g15: LineSegment StartX=28.21 StartY=-42.725 StartZ=0 EndX=28.21 EndY=-30.725 EndZ=0
  constraints (48):
    c: Coincident(g0,g1)
    c: Coincident(g1,g2)
    c: Coincident(g2,g3)
    c: Coincident(g3,g0)
    c: Horizontal(g0)
    c: Horizontal(g2)
    c: Vertical(g1)
    c: Vertical(g3)
    c: Coincident(g4,g5)
    c: Coincident(g5,g6)
    c: Coincident(g6,g7)
    c: Coincident(g7,g4)
    c: Horizontal(g4)
    c: Horizontal(g6)
    c: Vertical(g5)
    c: Vertical(g7)
    c: Coincident(g8,g9)
    c: Coincident(g9,g10)
    c: Coincident(g10,g11)
    c: Coincident(g11,g8)
    c: Horizontal(g8)
    c: Horizontal(g10)
    c: Vertical(g9)
    c: Vertical(g11)
    c: Coincident(g12,g13)
    c: Coincident(g13,g14)
    c: Coincident(g14,g15)
    c: Coincident(g15,g12)
    c: Horizontal(g12)
    c: Horizontal(g14)
    c: Vertical(g13)
    c: Vertical(g15)
    c: Symmetric(g5,g6,g-5)
    c: Symmetric(g10,g9,g-6)
    c: Symmetric(g0,g0,g-5)
    c: Symmetric(g12,g12,g-6)
    c: Equal(g3,g7)
    c: Equal(g7,g11)
    c: Equal(g11,g15)
    c: Equal(g4,g0)
    c: Equal(g0,g12)
    c: Equal(g12,g8)
    c: DistanceX(g0,g0) = 2
    c: DistanceY(g1,g1) = 12
    c: DistanceY(g-5,g5) = 0.2
    c: Horizontal(g5,g10)
    c: DistanceY(g-5,g1) = 0.2
    c: Horizontal(g1,g14)
FEATURE [PartDesign::Pad] Pad006  label="CoverLockingBarPad"
  BaseFeature = -> Pocket009
  Length = 6.2
  Length2 = 100
  Placement = pos=(50.925,29.21,49) rot=(0,0,1;1.5708rad)
  Profile = -> Sketch021
  Type = 0
FEATURE [Sketcher::SketchObject] Sketch022  label="LeftLockingLatch"
  ExternalGeometry = -> [Pad006]
  MapMode = 5
  Placement = pos=(50.925,59.42,49) rot=(0,0.707107,0.707107;3.14159rad)
  Support = -> [Pad006]
  sketch-geometry (8):
    g0: LineSegment StartX=-42.275 StartY=-3 StartZ=0 EndX=-30.275 EndY=-3 EndZ=0
    g1: LineSegment StartX=-30.275 StartY=-3 StartZ=0 EndX=-30.275 EndY=-5 EndZ=0
    g2: LineSegment StartX=-30.275 StartY=-5 StartZ=0 EndX=-42.275 EndY=-5 EndZ=0
    g3: LineSegment StartX=-42.275 StartY=-5 StartZ=0 EndX=-42.275 EndY=-3 EndZ=0
    g4: LineSegment StartX=30.725 StartY=-3 StartZ=0 EndX=42.725 EndY=-3 EndZ=0
    g5: LineSegment StartX=42.725 StartY=-3 StartZ=0 EndX=42.725 EndY=-5 EndZ=0
    g6: LineSegment StartX=42.725 StartY=-5 StartZ=0 EndX=30.725 EndY=-5 EndZ=0
    g7: LineSegment StartX=30.725 StartY=-5 StartZ=0 EndX=30.725 EndY=-3 EndZ=0
  constraints (24):
    c: Coincident(g0,g1)
    c: Coincident(g1,g2)
    c: Coincident(g2,g3)
    c: Coincident(g3,g0)
    c: Horizontal(g0)
    c: Horizontal(g2)
    c: Vertical(g1)
    c: Vertical(g3)
    c: Coincident(g4,g5)
    c: Coincident(g5,g6)
    c: Coincident(g6,g7)
    c: Coincident(g7,g4)
    c: Horizontal(g4)
    c: Horizontal(g6)
    c: Vertical(g5)
    c: Vertical(g7)
    c: Vertical(g0,g-3)
    c: Vertical(g-4,g0)
    c: Vertical(g-5,g4)
    c: Vertical(g-6,g4)
    c: Horizontal(g0,g4)
    c: Horizontal(g1,g6)
    c: Distance(g1) = 2
    c: DistanceY(g0,g-4) = 3
FEATURE [PartDesign::Pad] Pad007  label="LeftLockingLatchPad"
  BaseFeature = -> Pad006
  Length = 1
  Length2 = 100
  Placement = pos=(50.925,29.21,49) rot=(0,0,1;1.5708rad)
  Profile = -> Sketch022
  Type = 0
FEATURE [Sketcher::SketchObject] Sketch023  label="RightLockingLatch"
  ExternalGeometry = -> [Pad007]
  MapMode = 5
  Placement = pos=(50.925,-1,49) rot=(1,0,0;1.5708rad)
  Support = -> [Pad007]
  sketch-geometry (8):
    g0: LineSegment StartX=-42.725 StartY=-3 StartZ=0 EndX=-30.725 EndY=-3 EndZ=0
    g1: LineSegment StartX=-30.725 StartY=-3 StartZ=0 EndX=-30.725 EndY=-5 EndZ=0
    g2: LineSegment StartX=-30.725 StartY=-5 StartZ=0 EndX=-42.725 EndY=-5 EndZ=0
    g3: LineSegment StartX=-42.725 StartY=-5 StartZ=0 EndX=-42.725 EndY=-3 EndZ=0
    g4: LineSegment StartX=30.275 StartY=-3 StartZ=0 EndX=42.275 EndY=-3 EndZ=0
    g5: LineSegment StartX=42.275 StartY=-3 StartZ=0 EndX=42.275 EndY=-5 EndZ=0
    g6: LineSegment StartX=42.275 StartY=-5 StartZ=0 EndX=30.275 EndY=-5 EndZ=0
    g7: LineSegment StartX=30.275 StartY=-5 StartZ=0 EndX=30.275 EndY=-3 EndZ=0
  constraints (24):
    c: Coincident(g0,g1)
    c: Coincident(g1,g2)
    c: Coincident(g2,g3)
    c: Coincident(g3,g0)
    c: Horizontal(g0)
    c: Horizontal(g2)
    c: Vertical(g1)
    c: Vertical(g3)
    c: Coincident(g4,g5)
    c: Coincident(g5,g6)
    c: Coincident(g6,g7)
    c: Coincident(g7,g4)
    c: Horizontal(g4)
    c: Horizontal(g6)
    c: Vertical(g5)
    c: Vertical(g7)
    c: Vertical(g0,g-3)
    c: Vertical(g0,g-4)
    c: Vertical(g4,g-5)
    c: Vertical(g4,g-6)
    c: Horizontal(g0,g4)
    c: Distance(g1) = 2
    c: DistanceY(g0,g-4) = 3
    c: Equal(g7,g1)
FEATURE [PartDesign::Pad] Pad008  label="RightLockingLatchPad"
  BaseFeature = -> Pad007
  Length = 1
  Length2 = 100
  Placement = pos=(50.925,29.21,49) rot=(0,0,1;1.5708rad)
  Profile = -> Sketch023
  Type = 0
FEATURE [Sketcher::SketchObject] Sketch024  label="CarHoleGuide"
  ExternalGeometry = -> [Pocket007]
  MapMode = 5
  Placement = pos=(0,61.62,0) rot=(0,0.707107,0.707107;3.14159rad)
  Support = -> [Pocket007]
  sketch-geometry (4):
    g0: ArcOfCircle CenterX=-44.86 CenterY=5.5 CenterZ=0 NormalX=0 NormalY=0 NormalZ=1 AngleXU=0 Radius=3.5 StartAngle=1.5708 EndAngle=4.71239
    g1: ArcOfCircle CenterX=-31.26 CenterY=5.5 CenterZ=0 NormalX=0 NormalY=0 NormalZ=1 AngleXU=0 Radius=3.5 StartAngle=4.71239 EndAngle=7.85398
    g2: LineSegment StartX=-44.86 StartY=2 StartZ=0 EndX=-31.26 EndY=2 EndZ=0
    g3: LineSegment StartX=-44.86 StartY=9 StartZ=0 EndX=-31.26 EndY=9 EndZ=0
  constraints (9):
    c: Tangent(g0,g3) = 1.5708
    c: Tangent(g0,g2) = -1.5708
    c: Tangent(g2,g1) = -1.5708
    c: Tangent(g3,g1) = 1.5708
    c: Horizontal(g2)
    c: Equal(g0,g1)
    c: Symmetric(g-4,g-3,g1)
    c: Symmetric(g-3,g-4,g0)
    c: DistanceY(g-3,g0) = 2
FEATURE [PartDesign::Pocket] Pocket010  label="CardHoleGuidePocket"
  BaseFeature = -> Pocket007
  Length = 1.4
  Length2 = 100
  Profile = -> Sketch024
  Type = 0
FEATURE [Sketcher::SketchObject] Sketch025  label="FrontGuide"
  ExternalGeometry = -> [Pocket010]
  MapMode = 5
  Placement = pos=(-3.2,0,0) rot=(0.57735,-0.57735,-0.57735;2.0944rad)
  Support = -> [Pocket010]
  sketch-geometry (4):
    g0: ArcOfCircle CenterX=-35.5 CenterY=6.6 CenterZ=0 NormalX=0 NormalY=0 NormalZ=1 AngleXU=0 Radius=3 StartAngle=1.5708 EndAngle=4.71239
    g1: ArcOfCircle CenterX=-20.5 CenterY=6.6 CenterZ=0 NormalX=0 NormalY=0 NormalZ=1 AngleXU=0 Radius=3 StartAngle=4.71239 EndAngle=7.85398
    g2: LineSegment StartX=-35.5 StartY=3.6 StartZ=0 EndX=-20.5 EndY=3.6 EndZ=0
    g3: LineSegment StartX=-35.5 StartY=9.6 StartZ=0 EndX=-20.5 EndY=9.6 EndZ=0
  constraints (9):
    c: Tangent(g0,g3) = 1.5708
    c: Tangent(g0,g2) = -1.5708
    c: Tangent(g2,g1) = -1.5708
    c: Tangent(g3,g1) = 1.5708
    c: Horizontal(g2)
    c: Equal(g0,g1)
    c: DistanceY(g0,g0) = 3
    c: Coincident(g0,g-3)
    c: Vertical(g1,g-4)
FEATURE [PartDesign::Pocket] Pocket011  label="FrontGuidePocket"
  BaseFeature = -> Pocket010
  Length = 1
  Length2 = 100
  Profile = -> Sketch025
  Type = 0
FEATURE [PartDesign::ShapeBinder] ShapeBinder002  label="ButtonShapeBinder"
  Support = -> [Sketch]
FEATURE [Sketcher::SketchObject] Sketch026  label="ButtonBase"
  ExternalGeometry = -> [ShapeBinder002]
  MapMode = 5
  Placement = pos=(0,0,0) rot=(1,0,0;1.5708rad)
  Support = -> [XZ_Plane003]
  sketch-geometry (1):
    g0: Circle CenterX=28.8 CenterY=9.2 CenterZ=0 NormalX=0 NormalY=0 NormalZ=1 AngleXU=0 Radius=3.8
  constraints (3):
    c: Radius(g0) = 3.8
    c: Vertical(g0,g-3)
    c: DistanceY(g-3,g0) = 9.2
FEATURE [PartDesign::Pad] Pad009  label="ButtonBasePad"
  Length = 3
  Length2 = 100
  Placement = pos=(0,0,0) rot=(1,0,0;1.5708rad)
  Profile = -> Sketch026
  Type = 0
FEATURE [Sketcher::SketchObject] Sketch027  label="ButtonBody"
  ExternalGeometry = -> [Pad009]
  MapMode = 5
  Placement = pos=(0,-3,0) rot=(1,0,0;1.5708rad)
  Support = -> [Pad009]
  sketch-geometry (1):
    g0: Circle CenterX=28.8 CenterY=9.2 CenterZ=0 NormalX=0 NormalY=0 NormalZ=1 AngleXU=0 Radius=3.2
  constraints (2):
    c: Coincident(g0,g-3)
    c: Radius(g0) = 3.2
FEATURE [PartDesign::Pad] Pad010  label="ButtonBodyPad"
  BaseFeature = -> Pad009
  Length = 2.6
  Length2 = 100
  Placement = pos=(0,0,0) rot=(1,0,0;1.5708rad)
  Profile = -> Sketch027
  Type = 0
FEATURE [PartDesign::Fillet] Fillet  label="FilletButtonEdge"
  Base = -> Pad010 [Edge6]
  BaseFeature = -> Pad010
  Placement = pos=(0,0,0) rot=(1,0,0;1.5708rad)
  Radius = 1
FEATURE [Sketcher::SketchObject] Sketch028  label="LowerSideSunken"
  ExternalGeometry = -> [ShapeBinder,Pocket011]
  MapMode = 5
  Placement = pos=(50.925,29.21,19) rot=(0,0,1;1.5708rad)
  Support = -> [DatumPlane]
  sketch-geometry (4):
    g0: LineSegment StartX=-11.21 StartY=52.125 StartZ=0 EndX=8.79 EndY=52.125 EndZ=0
    g1: LineSegment StartX=8.79 StartY=52.125 StartZ=0 EndX=8.79 EndY=51.125 EndZ=0
    g2: LineSegment StartX=8.79 StartY=51.125 StartZ=0 EndX=-11.21 EndY=51.125 EndZ=0
    g3: LineSegment StartX=-11.21 StartY=51.125 StartZ=0 EndX=-11.21 EndY=52.125 EndZ=0
  constraints (12):
    c: Coincident(g0,g1)
    c: Coincident(g1,g2)
    c: Coincident(g2,g3)
    c: Coincident(g3,g0)
    c: Horizontal(g0)
    c: Horizontal(g2)
    c: Vertical(g1)
    c: Vertical(g3)
    c: Symmetric(g0,g0,g-3)
    c: PointOnObject(g1,g-4)
    c: DistanceY(g3,g3) = 1
    c: DistanceX(g0,g0) = 20
FEATURE [PartDesign::Pocket] Pocket012  label="LowerSideSunkenPocket"
  BaseFeature = -> Pocket011
  Length = 17
  Length2 = 100
  Profile = -> Sketch028
  Type = 0
FEATURE [PartDesign::Fillet] Fillet001  label="FilletOuter"
  Base = -> Pocket012 [Edge20,Edge2,Edge26,Edge3]
  BaseFeature = -> Pocket012
  Radius = 4
FEATURE [PartDesign::Fillet] Fillet002  label="FilletInner"
  Base = -> Fillet001 [Edge94,Edge97,Edge138,Edge134]
  BaseFeature = -> Fillet001
  Radius = 1
FEATURE [PartDesign::Fillet] Fillet003  label="FilletBottom"
  Base = -> Fillet002 [Edge94]
  BaseFeature = -> Fillet002
  Radius = 1
FEATURE [PartDesign::Chamfer] Chamfer  label="ChamferLower"
  Base = -> Fillet003 [Edge84,Edge253,Edge247,Edge251,Edge249]
  BaseFeature = -> Fillet003
  Size = 0.6
FEATURE [PartDesign::Chamfer] Chamfer001  label="ChamferCard"
  Base = -> Chamfer [Edge119,Edge253,Edge252,Edge249,Edge247]
  BaseFeature = -> Chamfer
  Size = 0.6
FEATURE [PartDesign::Chamfer] Chamfer002  label="ChamferButtonHole"
  Base = -> Chamfer001 [Edge157,Edge158]
  BaseFeature = -> Chamfer001
  Size = 0.4
FEATURE [PartDesign::Fillet] Fillet004  label="FilletCoverOuter"
  Base = -> Pad008 [Edge2,Edge8,Edge5,Edge1]
  BaseFeature = -> Pad008
  Placement = pos=(50.925,29.21,49) rot=(0,0,1;1.5708rad)
  Radius = 4
FEATURE [PartDesign::Fillet] Fillet005  label="FilletCoverInner"
  Base = -> Fillet004 [Edge57,Edge59,Edge94,Edge93]
  BaseFeature = -> Fillet004
  Placement = pos=(50.925,29.21,49) rot=(0,0,1;1.5708rad)
  Radius = 1
FEATURE [PartDesign::Fillet] Fillet006  label="FilletCoverTop"
  Base = -> Fillet005 [Edge123]
  BaseFeature = -> Fillet005
  Placement = pos=(50.925,29.21,49) rot=(0,0,1;1.5708rad)
  Radius = 1
FEATURE [PartDesign::Fillet] Fillet007  label="FilletLockingBar"
  Base = -> Fillet006 [Edge213,Edge193,Edge196,Edge216]
  BaseFeature = -> Fillet006
  Placement = pos=(50.925,29.21,49) rot=(0,0,1;1.5708rad)
  Radius = 0.8
FEATURE [PartDesign::Fillet] Fillet008  label="FilletLockingLatchBottom"
  Base = -> Fillet007 [Edge254,Edge256,Edge255,Edge94]
  BaseFeature = -> Fillet007
  Placement = pos=(50.925,29.21,49) rot=(0,0,1;1.5708rad)
  Radius = 0.8
FEATURE [PartDesign::Fillet] Fillet009  label="FilletLockingLatchTop"
  Base = -> Fillet008 [Edge235,Edge214,Edge234,Edge7]
  BaseFeature = -> Fillet008
  Placement = pos=(50.925,29.21,49) rot=(0,0,1;1.5708rad)
  Radius = 0.8
FEATURE [Sketcher::SketchObject] Sketch029  label="ButtonHole"
  ExternalGeometry = -> [Fillet]
  MapMode = 5
  Placement = pos=(0,0,0) rot=(-1,0,0;1.5708rad)
  Support = -> [Fillet]
  sketch-geometry (1):
    g0: Circle CenterX=28.8 CenterY=-9.2 CenterZ=0 NormalX=0 NormalY=0 NormalZ=1 AngleXU=0 Radius=2
  constraints (2):
    c: Coincident(g0,g-3)
    c: Radius(g0) = 2
FEATURE [PartDesign::Pocket] Pocket013  label="ButtonHolePocket"
  BaseFeature = -> Fillet
  Length = 1
  Length2 = 100
  Placement = pos=(0,0,0) rot=(1,0,0;1.5708rad)
  Profile = -> Sketch029
  Type = 0
FEATURE [PartDesign::Body] Body003  label="ButtonBlock"
  Group = -> [ShapeBinder002,Sketch026,Pad009,Sketch027,Pad010,Fillet,Sketch029,Pocket013]
  Origin = -> Origin003
  Placement = pos=(0,1.4,0) rot=(0,0,1;0rad)
  Tip = -> Pocket013
FEATURE [PartDesign::Fillet] Fillet010  label="FilletSupport"
  Base = -> Chamfer002 [Edge204,Edge203,Edge206,Edge205]
  BaseFeature = -> Chamfer002
  Radius = 1.4
FEATURE [PartDesign::Fillet] Fillet011  label="FilletCoverSupport"
  Base = -> Fillet009 [Edge103,Edge104,Edge100,Edge101]
  BaseFeature = -> Fillet009
  Placement = pos=(50.925,29.21,49) rot=(0,0,1;1.5708rad)
  Radius = 1.6
FEATURE [PartDesign::Fillet] Fillet012  label="FilletCoverLockingBar"
  Base = -> Fillet011 [Edge6,Edge13,Edge14,Edge21]
  BaseFeature = -> Fillet011
  Placement = pos=(50.925,29.21,49) rot=(0,0,1;1.5708rad)
  Radius = 2
FEATURE [PartDesign::Fillet] Fillet013  label="FilletInnerBottom"
  Base = -> Fillet010 [Edge5]
  BaseFeature = -> Fillet010
  Radius = 1
FEATURE [PartDesign::Fillet] Fillet014  label="FilletInnerUpper"
  Base = -> Fillet013 [Edge102,Edge91,Edge55,Edge126,Edge46]
  BaseFeature = -> Fillet013
  Radius = 1
FEATURE [PartDesign::Fillet] Fillet015  label="FilletInnerSoundHole"
  Base = -> Fillet012 [Edge38]
  BaseFeature = -> Fillet012
  Placement = pos=(50.925,29.21,49) rot=(0,0,1;1.5708rad)
  Radius = 1
FEATURE [Sketcher::SketchObject] Sketch030  label="LEDHole"
  ExternalGeometry = -> [ShapeBinder001]
  MapMode = 5
  Placement = pos=(50.925,29.21,48) rot=(0.707107,0.707107,0;3.14159rad)
  Support = -> [Fillet015]
  sketch-geometry (4):
    g0: Circle CenterX=-16.21 CenterY=27.875 CenterZ=0 NormalX=0 NormalY=0 NormalZ=1 AngleXU=0 Radius=1.6
    g1: Circle CenterX=-12.21 CenterY=27.875 CenterZ=0 NormalX=0 NormalY=0 NormalZ=1 AngleXU=0 Radius=1.6
    g2: Circle CenterX=-8.21 CenterY=27.875 CenterZ=0 NormalX=0 NormalY=0 NormalZ=1 AngleXU=0 Radius=1.6
    g3: Circle CenterX=-4.21 CenterY=27.875 CenterZ=0 NormalX=0 NormalY=0 NormalZ=1 AngleXU=0 Radius=1.6
  constraints (8):
    c: Coincident(g0,g-3)
    c: Coincident(g1,g-4)
    c: Coincident(g2,g-5)
    c: Coincident(g3,g-6)
    c: Equal(g0,g1)
    c: Equal(g1,g2)
    c: Equal(g2,g3)
    c: Radius(g0) = 1.6
FEATURE [PartDesign::Pocket] Pocket014  label="LEDHolePoket"
  BaseFeature = -> Fillet015
  Length = 1.6
  Length2 = 100
  Placement = pos=(50.925,29.21,49) rot=(0,0,1;1.5708rad)
  Profile = -> Sketch030
  Type = 0
FEATURE [PartDesign::Body] Body002  label="CoverBlock"
  Group = -> [ShapeBinder001,DatumPlane008,Sketch012,Pad003,Sketch017,Pad004,DatumPlane009,Sketch018,Pad005,DatumPlane010,Sketch019,Pocket008,Sketch020,Pocket009,DatumPlane011,Sketch021,Pad006,Sketch022,Pad007,Sketch023,Pad008,Fillet004,Fillet005,Fillet006,Fillet007,Fillet008,Fillet009,Fillet011,Fillet012,Fillet015,Sketch030,Pocket014]
  Origin = -> Origin002
  Placement = pos=(0,0,7) rot=(0,0,1;0rad)
  Tip = -> Pocket014
FEATURE [Mesh::Feature] Mesh001  label="Cover (Meshed)"
  Placement = pos=(0,0,-30) rot=(0,0,1;0rad)
FEATURE [Mesh::Feature] Mesh003  label="Body (Meshed)"
FEATURE [Mesh::Feature] Mesh  label="Button (Meshed)"
FEATURE [PartDesign::Fillet] Fillet016
  Base = -> Fillet014 [Edge437,Edge431,Edge433,Edge435]
  BaseFeature = -> Fillet014
  Radius = 0.6
FEATURE [Sketcher::SketchObject] Sketch031
  ExternalGeometry = -> [Fillet016]
  MapMode = 5
  Placement = pos=(0,-3.2,0) rot=(1,0,0;1.5708rad)
  Support = -> [Fillet016]
  sketch-geometry (1):
    g0: Circle CenterX=2.8 CenterY=5 CenterZ=0 NormalX=0 NormalY=0 NormalZ=1 AngleXU=0 Radius=0.6
  constraints (3):
    c: DistanceY(g-3,g0) = 4
    c: DistanceX(g-3,g0) = 2
    c: Radius(g0) = 0.6
FEATURE [PartDesign::Pocket] Pocket015
  BaseFeature = -> Fillet016
  Length = 5
  Length2 = 100
  Profile = -> Sketch031
  Type = 1
FEATURE [Sketcher::SketchObject] Sketch032
  ExternalGeometry = -> [Pocket015]
  MapMode = 5
  Placement = pos=(-3.2,0,0) rot=(0.57735,-0.57735,-0.57735;2.0944rad)
  Support = -> [Pocket015]
  sketch-geometry (1):
    g0: Circle CenterX=-2.8 CenterY=5 CenterZ=0 NormalX=0 NormalY=0 NormalZ=1 AngleXU=0 Radius=0.6
  constraints (3):
    c: Radius(g0) = 0.6
    c: DistanceX(g0,g-3) = 2
    c: DistanceY(g-3,g0) = 4
FEATURE [PartDesign::Pocket] Pocket016
  BaseFeature = -> Pocket015
  Length = 5
  Length2 = 100
  Profile = -> Sketch032
  Type = 1
FEATURE [PartDesign::Body] Body001  label="BodyBlock"
  Group = -> [ShapeBinder,Sketch001,Pad,DatumPlane,Sketch002,Pocket,DatumPlane001,Sketch003,Pad001,DatumPlane002,Sketch004,Pad002,DatumPlane003,DatumPlane004,DatumPlane005,Sketch005,Pocket001,Sketch006,Pocket002,Sketch007,Pocket003,DatumPlane006,DatumPlane007,Sketch008,Pocket004,Sketch009,Pocket005,Sketch010,Pocket006,Sketch011,Pocket007,Sketch024,Pocket010,Sketch025,Pocket011,Sketch028,Pocket012,Fillet001,+13 more]
  Origin = -> Origin001
  Tip = -> Pocket016
FEATURE [Mesh::Feature] Mesh004  label="Body-wt-Hole (Meshed)"
